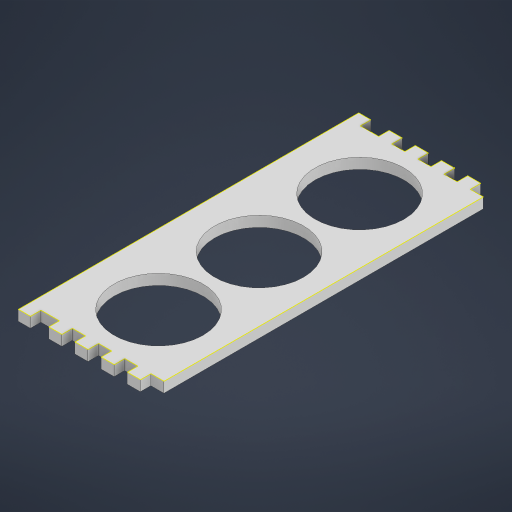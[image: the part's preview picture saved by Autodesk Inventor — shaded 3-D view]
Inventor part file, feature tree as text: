
AUTODESK INVENTOR PART (.ipt)
format: ipt  version: 2023 (Build 270158030, 158C)  size: 266,240 bytes
history: native  units: mm
features: sketch x3, extrude x2, plane x1, projected_geometry x1
ambient origin geometry x8: Origin, YZ Plane, XZ Plane, XY Plane, X Axis, Y Axis, Z Axis, Center Point
bodies: Solid1 (feature_tree)
feature tree (7):
  extrude  "Extrusion1"  TaperAngle=30.0deg  [1 undecoded]
  plane  "Work Plane1"
  sketch  "Sketch5"  dims[d16=34.0mm d17=34.0mm]
  extrude  "Extrusion4"  Depth=34.0mm
  sketch  "Sketch1"  dims[d0=4.0mm d1=0.0mm d2=30.0deg]
  projected_geometry  "Projected Loop2"
  sketch  "Sketch6"  dims[d18=34.0mm d19=5.5mm d20=0.0mm]
note: 1 required parameter value undecoded (feature->parameter linkage not recoverable at this tier; creation-order binding heuristic only, values carry confidence <= 0.55)
